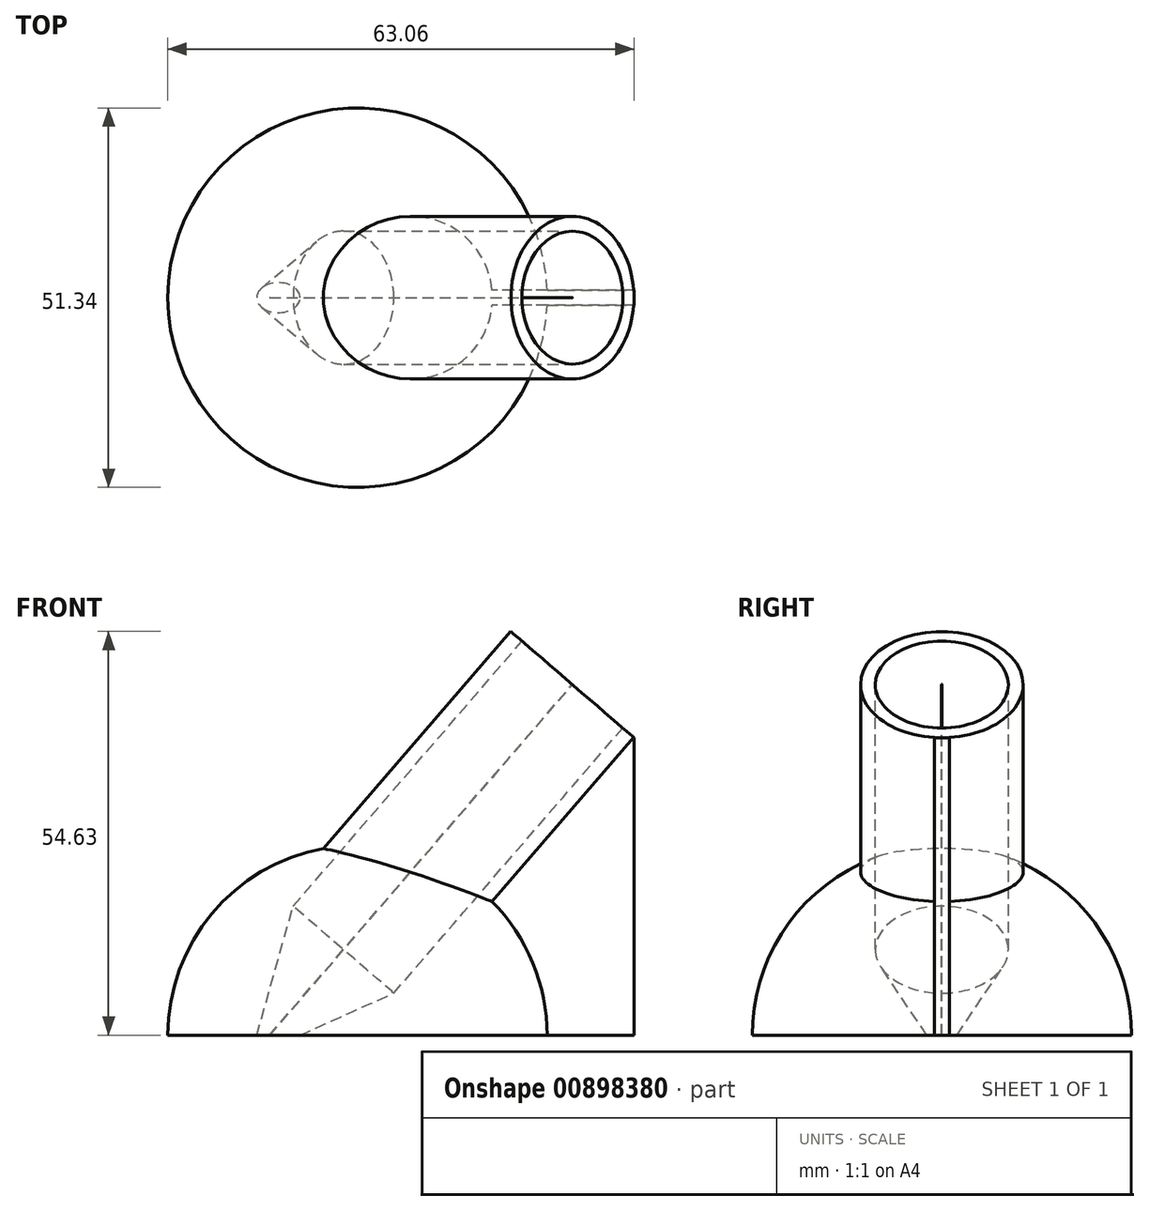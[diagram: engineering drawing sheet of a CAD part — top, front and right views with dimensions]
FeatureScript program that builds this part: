
annotation { "Feature Type Name" : "Feature", "Feature Type Description" : "" }
export const myFeature = defineFeature(function(context is Context, id is Id, definition is map)
    precondition{}
    {
        {
            var Q0;
            Q0=qCreatedBy(makeId("Front.planeOp"),FACE);
            var sketch = newSketch(context, id + "F0", { "sketchPlane" : qUnion([Q0])});
            skLineSegment(sketch, "E0", {"start": v(2.64, 0) * mm, "end": v(37.4, 40.25) * mm});
            skLineSegment(sketch, "E1", {"start": v(37.4, 40.25) * mm, "end": v(20.74, 54.63) * mm});
            skLineSegment(sketch, "E2", {"start": v(20.74, 54.63) * mm, "end": v(-14.01, 14.38) * mm});
            skLineSegment(sketch, "E3", {"start": v(-14.01, 14.38) * mm, "end": v(2.64, 0) * mm});
            skLineSegment(sketch, "E4", {"start": v(-5.68, 7.19) * mm, "end": v(29.07, 47.44) * mm});
            skSolve(sketch);
        }
        {
            var Q0;
            {var subQ0=sQuery(id+"F0.wireOp",EDGE,"E0");Q0=makeQuery(id+"F0.imprint","IMPRINT",FACE,{"disambiguationData":[TD([[makeQuery(id+"F0.imprint","IMPRINT",EDGE,{"derivedFrom":subQ0}),1.0]])]});}
            var Q1;
            Q1=sQuery(id+"F0.wireOp",EDGE,"E4");
            revolve(context, id + "F1", {"surfaceOperationType" : NewSurfaceOperationType.NEW, "entities" : qUnion([Q0]), "axis" : qUnion([Q1]), "revolveType" : RevolveType.FULL});
        }
        {
            var Q0;
            Q0=qCreatedBy(makeId("Front.planeOp"),FACE);
            var sketch = newSketch(context, id + "F2", { "sketchPlane" : qUnion([Q0])});
            skLineSegment(sketch, "E5", {"start": v(0, 25.67) * mm, "end": v(0, 0) * mm});
            skLineSegment(sketch, "E6", {"start": v(0, 0) * mm, "end": v(25.67, 0) * mm});
            skArc(sketch, "E7", {"start": v(25.67, 0) * mm, "mid": v(18.15, 18.15) * mm, "end": v(0, 25.67) * mm});
            skSolve(sketch);
        }
        {
            var Q0;
            Q0=makeQuery(id+"F2.imprint","IMPRINT",FACE,{"disambiguationData":[TD([[makeQuery(id+"F2.imprint","IMPRINT",EDGE,{"derivedFrom":sQuery(id+"F2.wireOp",EDGE,"E5")}),1.0]])]});
            var Q1;
            Q1=sQuery(id+"F2.wireOp",EDGE,"E5");
            revolve(context, id + "F3", {"operationType" : NewBodyOperationType.ADD, "surfaceOperationType" : NewSurfaceOperationType.NEW, "entities" : qUnion([Q0]), "axis" : qUnion([Q1]), "revolveType" : RevolveType.FULL});
        }
        {
            var Q0;
            Q0=qCreatedBy(makeId("Front.planeOp"),FACE);
            var sketch = newSketch(context, id + "F4", { "sketchPlane" : qUnion([Q0])});
            skLineSegment(sketch, "E8", {"start": v(37.4, 40.25) * mm, "end": v(37.4, 0) * mm});
            skLineSegment(sketch, "E9", {"start": v(37.4, 0) * mm, "end": v(25.67, 0) * mm});
            skLineSegment(sketch, "E10", {"start": v(-4.62, 25.25) * mm, "end": v(20.74, 54.63) * mm});
            skLineSegment(sketch, "E11", {"start": v(37.4, 40.25) * mm, "end": v(18.24, 18.06) * mm});
            skLineSegment(sketch, "E12.0", {"start": v(37.4, 40.25) * mm, "end": v(20.74, 54.63) * mm});
            skLineSegment(sketch, "E13", {"start": v(29.07, 47.44) * mm, "end": v(6.94, 21.81) * mm});
            skLineSegment(sketch, "E14", {"start": v(6.94, 21.81) * mm, "end": v(6.94, 0) * mm});
            skLineSegment(sketch, "E15", {"start": v(6.94, 0) * mm, "end": v(25.67, 0) * mm});
            skSolve(sketch);
        }
        {
            var Q0;
            {var subQ2=sQuery(id+"F4.wireOp",EDGE,"E8");Q0=makeQuery(id+"F4.imprint","IMPRINT",FACE,{"disambiguationData":[TD([[makeQuery(id+"F4.imprint","IMPRINT",EDGE,{"derivedFrom":subQ2}),-1.0]])]});}
            extrude(context, id + "F5", {"entities" : qUnion([Q0]), "operationType" : NewBodyOperationType.ADD, "depth" : 2 * mm, "offsetDistance" : 25 * mm, "symmetric" : true});
        }
        {
            var Q0;
            Q0=qCreatedBy(makeId("Front.planeOp"),FACE);
            var sketch = newSketch(context, id + "F6", { "sketchPlane" : qUnion([Q0])});
            skLineSegment(sketch, "E16", {"start": v(-4.62, 25.25) * mm, "end": v(20.74, 54.63) * mm});
            skLineSegment(sketch, "E17.0", {"start": v(37.36, 40.28) * mm, "end": v(18.2, 18.08) * mm});
            skLineSegment(sketch, "E18.0", {"start": v(37.36, 40.28) * mm, "end": v(20.74, 54.63) * mm});
            skLineSegment(sketch, "E19", {"start": v(22.25, 53.32) * mm, "end": v(-8.72, 17.45) * mm});
            skLineSegment(sketch, "E20", {"start": v(-8.72, 17.45) * mm, "end": v(-14.47, -2.95) * mm});
            skLineSegment(sketch, "E21", {"start": v(-14.47, -2.95) * mm, "end": v(4.87, 5.71) * mm});
            skLineSegment(sketch, "E22", {"start": v(4.87, 5.71) * mm, "end": v(35.84, 41.59) * mm});
            skLineSegment(sketch, "E23", {"start": v(35.84, 41.59) * mm, "end": v(22.25, 53.32) * mm});
            skLineSegment(sketch, "E24", {"start": v(-14.47, -2.95) * mm, "end": v(29.05, 47.45) * mm});
            skSolve(sketch);
        }
        {
            var Q0;
            Q0=makeQuery(id+"F6.imprint","IMPRINT",FACE,{"disambiguationData":[TD([[makeQuery(id+"F6.imprint","IMPRINT",EDGE,{"derivedFrom":sQuery(id+"F6.wireOp",EDGE,"E19")}),1.0]])]});
            var Q1;
            Q1=sQuery(id+"F0.wireOp",EDGE,"E4");
            revolve(context, id + "F7", {"operationType" : NewBodyOperationType.REMOVE, "surfaceOperationType" : NewSurfaceOperationType.NEW, "entities" : qUnion([Q0]), "axis" : qUnion([Q1]), "revolveType" : RevolveType.FULL, "oppositeDirection" : true});
        }
    });
